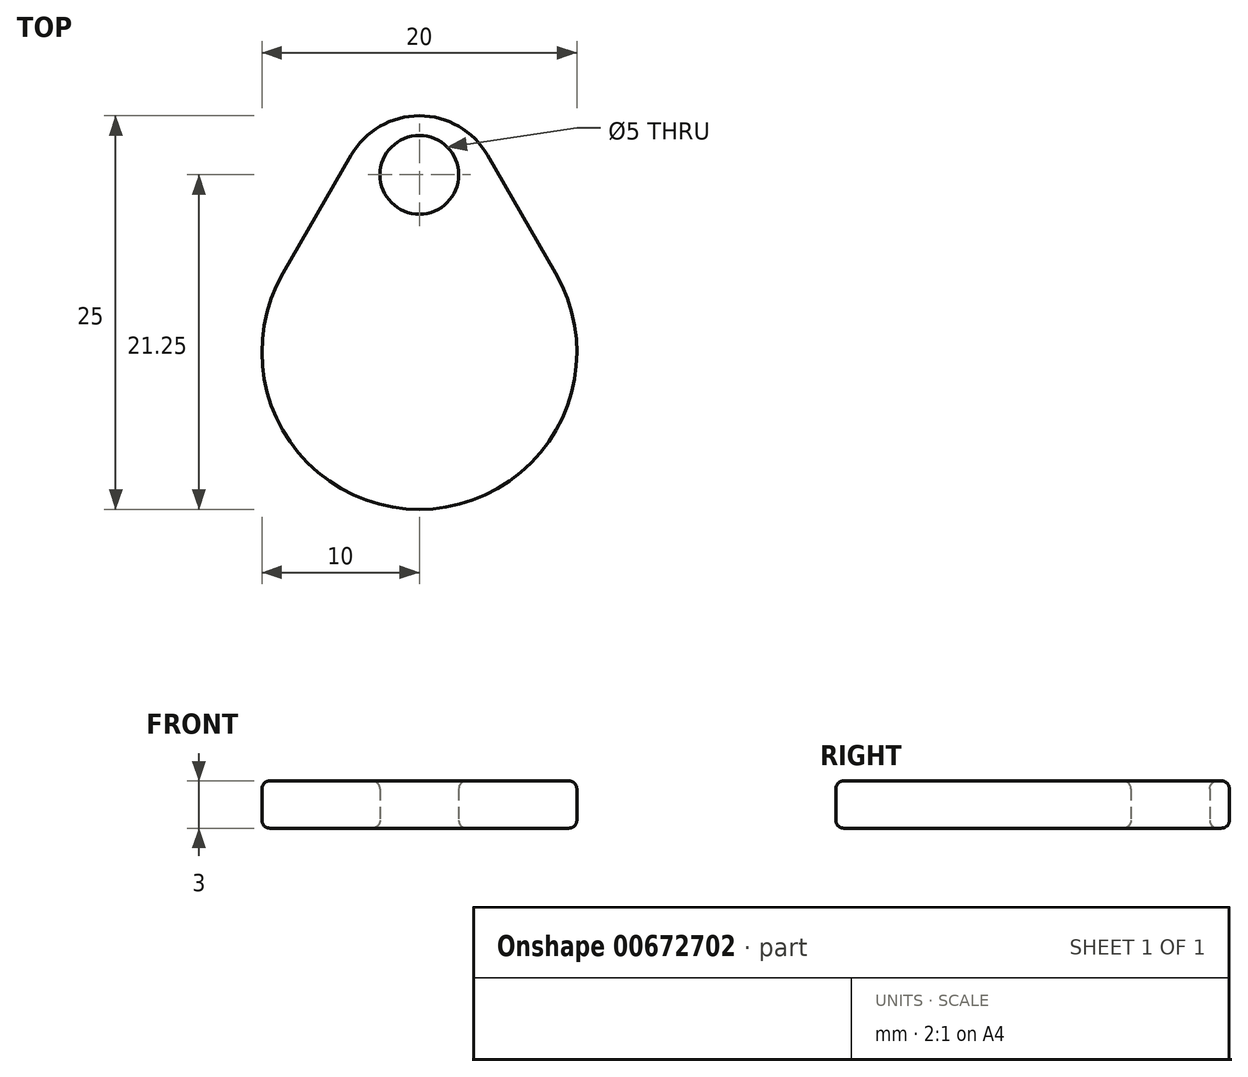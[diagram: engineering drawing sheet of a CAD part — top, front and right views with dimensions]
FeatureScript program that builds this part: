
annotation { "Feature Type Name" : "Feature", "Feature Type Description" : "" }
export const myFeature = defineFeature(function(context is Context, id is Id, definition is map)
    precondition{}
    {
        {
            var Q0;
            Q0=qCreatedBy(makeId("Top.planeOp"),FACE);
            var sketch = newSketch(context, id + "F0", { "sketchPlane" : qUnion([Q0])});
            skCircle(sketch, "E0", {"center": v(0, 0) * mm, "radius": 10 * mm});
            skCircle(sketch, "E1", {"center": v(0, 10) * mm, "radius": 5 * mm});
            skLineSegment(sketch, "E2", {"start": v(0, 10) * mm, "end": v(0, 15) * mm});
            skPoint(sketch, "E3", {"position": v(0, 11.25) * mm});
            skCircle(sketch, "E4", {"center": v(0, 11.25) * mm, "radius": 2.5 * mm});
            skArc(sketch, "E5.trimOffspring", {"start": v(1.91, 12.86) * mm, "mid": v(0, 13) * mm, "end": v(-1.91, 12.86) * mm});
            skLineSegment(sketch, "E6", {"start": v(-8.66, 5) * mm, "end": v(-4.33, 12.5) * mm});
            skLineSegment(sketch, "E7.MirrorCS", {"start": v(8.66, 5) * mm, "end": v(4.33, 12.5) * mm});
            skSolve(sketch);
        }
        {
            var Q0;
            {var subQ0=sQuery(id+"F0.wireOp",EDGE,"E0");var subQ1=makeQuery(id+"F0.imprint","INTERSECT",VERTEX,{"derivedFrom":[subQ0,sQuery(id+"F0.wireOp",EDGE,"E7.MirrorCS")]});Q0=makeQuery(id+"F0.imprint","IMPRINT",FACE,{"disambiguationData":[TD([[makeQuery(id+"F0.imprint","IMPRINT",EDGE,{"disambiguationData":[TD([[subQ1,-1.0]])],"derivedFrom":subQ0}),1.0]])]});}
            var Q1;
            {var subQ0=sQuery(id+"F0.wireOp",EDGE,"E6");Q1=makeQuery(id+"F0.imprint","IMPRINT",FACE,{"disambiguationData":[TD([[makeQuery(id+"F0.imprint","IMPRINT",EDGE,{"derivedFrom":subQ0}),-1.0]])]});}
            var Q2;
            {var subQ0=sQuery(id+"F0.wireOp",EDGE,"E1");var subQ1=sQuery(id+"F0.wireOp",EDGE,"E0");var subQ2=makeQuery(id+"F0.imprint","INTERSECT",VERTEX,{"disambiguationData":[OD(0.0)],"derivedFrom":[subQ1,subQ0]});Q2=makeQuery(id+"F0.imprint","IMPRINT",FACE,{"disambiguationData":[TD([[makeQuery(id+"F0.imprint","IMPRINT",EDGE,{"disambiguationData":[TD([[subQ2,-1.0]])],"derivedFrom":subQ1}),1.0]])]});}
            var Q3;
            {var subQ1=sQuery(id+"F0.wireOp",EDGE,"E1");var subQ6=sQuery(id+"F0.wireOp",EDGE,"E0");var subQ7=makeQuery(id+"F0.imprint","INTERSECT",VERTEX,{"disambiguationData":[OD(0.0)],"derivedFrom":[subQ6,subQ1]});Q3=makeQuery(id+"F0.imprint","IMPRINT",FACE,{"disambiguationData":[TD([[makeQuery(id+"F0.imprint","IMPRINT",EDGE,{"disambiguationData":[TD([[subQ7,-1.0]])],"derivedFrom":subQ6}),-1.0]])]});}
            var Q4;
            {var subQ0=sQuery(id+"F0.wireOp",EDGE,"E7.MirrorCS");Q4=makeQuery(id+"F0.imprint","IMPRINT",FACE,{"disambiguationData":[TD([[makeQuery(id+"F0.imprint","IMPRINT",EDGE,{"derivedFrom":subQ0}),1.0]])]});}
            var Q5;
            {var subQ4=sQuery(id+"F0.wireOp",EDGE,"E4");var subQ6=sQuery(id+"F0.wireOp",EDGE,"E0");var subQ8=makeQuery(id+"F0.imprint","INTERSECT",VERTEX,{"disambiguationData":[OD(1.0)],"derivedFrom":[subQ6,subQ4]});Q5=makeQuery(id+"F0.imprint","IMPRINT",FACE,{"disambiguationData":[TD([[makeQuery(id+"F0.imprint","IMPRINT",EDGE,{"disambiguationData":[TD([[subQ8,-1.0]])],"derivedFrom":subQ6}),-1.0]])]});}
            extrude(context, id + "F1", {"entities" : qUnion([Q0, Q1, Q2, Q3, Q4, Q5]), "depth" : 3 * mm, "offsetDistance" : 25 * mm});
        }
        {
            var Q0;
            Q0=makeQuery(id+"F1.opExtrude","CAP_EDGE",EDGE,{"disambiguationData":[OSD([sQuery(id+"F0.wireOp",EDGE,"E7.MirrorCS")])],"isStart":false});
            var Q1;
            Q1=makeQuery(id+"F1.opExtrude","CAP_EDGE",EDGE,{"disambiguationData":[OSD([sQuery(id+"F0.wireOp",EDGE,"E1")])],"isStart":false});
            var Q2;
            Q2=makeQuery(id+"F1.opExtrude","CAP_EDGE",EDGE,{"disambiguationData":[OSD([sQuery(id+"F0.wireOp",EDGE,"E1")])],"isStart":true});
            var Q3;
            Q3=makeQuery(id+"F1.opExtrude","CAP_EDGE",EDGE,{"disambiguationData":[OSD([sQuery(id+"F0.wireOp",EDGE,"E7.MirrorCS")])],"isStart":true});
            var Q4;
            {var subQ0=sQuery(id+"F0.wireOp",EDGE,"E0");Q4=makeQuery(id+"F1.opExtrude","CAP_EDGE",EDGE,{"disambiguationData":[OSD([subQ0]),TDD([makeQuery(id+"F0.imprint","IMPRINT",EDGE,{"disambiguationData":[TD([[makeQuery(id+"F0.imprint","INTERSECT",VERTEX,{"derivedFrom":[subQ0,sQuery(id+"F0.wireOp",EDGE,"E6")]}),-1.0]])],"derivedFrom":subQ0})])],"isStart":true});}
            var Q5;
            {var subQ0=sQuery(id+"F0.wireOp",EDGE,"E0");Q5=makeQuery(id+"F1.opExtrude","CAP_EDGE",EDGE,{"disambiguationData":[OSD([subQ0]),TDD([makeQuery(id+"F0.imprint","IMPRINT",EDGE,{"disambiguationData":[TD([[makeQuery(id+"F0.imprint","INTERSECT",VERTEX,{"derivedFrom":[subQ0,sQuery(id+"F0.wireOp",EDGE,"E6")]}),-1.0]])],"derivedFrom":subQ0})])],"isStart":false});}
            var Q6;
            Q6=makeQuery(id+"F1.opExtrude","CAP_EDGE",EDGE,{"disambiguationData":[OSD([sQuery(id+"F0.wireOp",EDGE,"E6")])],"isStart":false});
            var Q7;
            {var subQ0=sQuery(id+"F0.wireOp",EDGE,"E0");var subQ1=makeQuery(id+"F0.imprint","INTERSECT",VERTEX,{"derivedFrom":[subQ0,sQuery(id+"F0.wireOp",EDGE,"E2")]});Q7=makeQuery(id+"F1.opExtrude","CAP_EDGE",EDGE,{"disambiguationData":[OSD([subQ0]),TDD([makeQuery(id+"F0.imprint","IMPRINT",EDGE,{"disambiguationData":[TD([[subQ1,1.0]])],"derivedFrom":subQ0}),makeQuery(id+"F0.imprint","IMPRINT",EDGE,{"disambiguationData":[TD([[subQ1,-1.0]])],"derivedFrom":subQ0})])],"isStart":false});}
            var Q8;
            {var subQ0=sQuery(id+"F0.wireOp",EDGE,"E4");Q8=makeQuery(id+"F1.opExtrude","CAP_EDGE",EDGE,{"disambiguationData":[OSD([subQ0]),TDD([makeQuery(id+"F0.imprint","IMPRINT",EDGE,{"disambiguationData":[TD([[makeQuery(id+"F0.imprint","INTERSECT",VERTEX,{"disambiguationData":[OD(1.0)],"derivedFrom":[subQ0,sQuery(id+"F0.wireOp",EDGE,"E5.trimOffspring")]}),-1.0]])],"derivedFrom":subQ0})])],"isStart":false});}
            var Q9;
            Q9=makeQuery(id+"F1.opExtrude","CAP_EDGE",EDGE,{"disambiguationData":[OSD([sQuery(id+"F0.wireOp",EDGE,"E5.trimOffspring")])],"isStart":false});
            var Q10;
            {var subQ0=sQuery(id+"F0.wireOp",EDGE,"E4");Q10=makeQuery(id+"F1.opExtrude","CAP_EDGE",EDGE,{"disambiguationData":[OSD([subQ0]),TDD([makeQuery(id+"F0.imprint","IMPRINT",EDGE,{"disambiguationData":[TD([[makeQuery(id+"F0.imprint","INTERSECT",VERTEX,{"disambiguationData":[OD(0.0)],"derivedFrom":[subQ0,sQuery(id+"F0.wireOp",EDGE,"E5.trimOffspring")]}),1.0]])],"derivedFrom":subQ0})])],"isStart":false});}
            var Q11;
            {var subQ0=sQuery(id+"F0.wireOp",EDGE,"E0");var subQ1=makeQuery(id+"F0.imprint","INTERSECT",VERTEX,{"derivedFrom":[subQ0,sQuery(id+"F0.wireOp",EDGE,"E2")]});Q11=makeQuery(id+"F1.opExtrude","CAP_EDGE",EDGE,{"disambiguationData":[OSD([subQ0]),TDD([makeQuery(id+"F0.imprint","IMPRINT",EDGE,{"disambiguationData":[TD([[subQ1,1.0]])],"derivedFrom":subQ0}),makeQuery(id+"F0.imprint","IMPRINT",EDGE,{"disambiguationData":[TD([[subQ1,-1.0]])],"derivedFrom":subQ0})])],"isStart":true});}
            var Q12;
            {var subQ0=sQuery(id+"F0.wireOp",EDGE,"E4");Q12=makeQuery(id+"F1.opExtrude","CAP_EDGE",EDGE,{"disambiguationData":[OSD([subQ0]),TDD([makeQuery(id+"F0.imprint","IMPRINT",EDGE,{"disambiguationData":[TD([[makeQuery(id+"F0.imprint","INTERSECT",VERTEX,{"disambiguationData":[OD(0.0)],"derivedFrom":[subQ0,sQuery(id+"F0.wireOp",EDGE,"E5.trimOffspring")]}),1.0]])],"derivedFrom":subQ0})])],"isStart":true});}
            var Q13;
            Q13=makeQuery(id+"F1.opExtrude","CAP_EDGE",EDGE,{"disambiguationData":[OSD([sQuery(id+"F0.wireOp",EDGE,"E5.trimOffspring")])],"isStart":true});
            var Q14;
            {var subQ0=sQuery(id+"F0.wireOp",EDGE,"E4");Q14=makeQuery(id+"F1.opExtrude","CAP_EDGE",EDGE,{"disambiguationData":[OSD([subQ0]),TDD([makeQuery(id+"F0.imprint","IMPRINT",EDGE,{"disambiguationData":[TD([[makeQuery(id+"F0.imprint","INTERSECT",VERTEX,{"disambiguationData":[OD(1.0)],"derivedFrom":[subQ0,sQuery(id+"F0.wireOp",EDGE,"E5.trimOffspring")]}),-1.0]])],"derivedFrom":subQ0})])],"isStart":true});}
            var Q15;
            Q15=makeQuery(id+"F1.opExtrude","CAP_EDGE",EDGE,{"disambiguationData":[OSD([sQuery(id+"F0.wireOp",EDGE,"E6")])],"isStart":true});
            fillet(context, id + "F2", {"entities" : qUnion([Q0, Q1, Q2, Q3, Q4, Q5, Q6, Q7, Q8, Q9, Q10, Q11, Q12, Q13, Q14, Q15]), "radius" : 0.5 * mm, "tangentPropagation" : true, "allowEdgeOverflow" : false});
        }
    });
